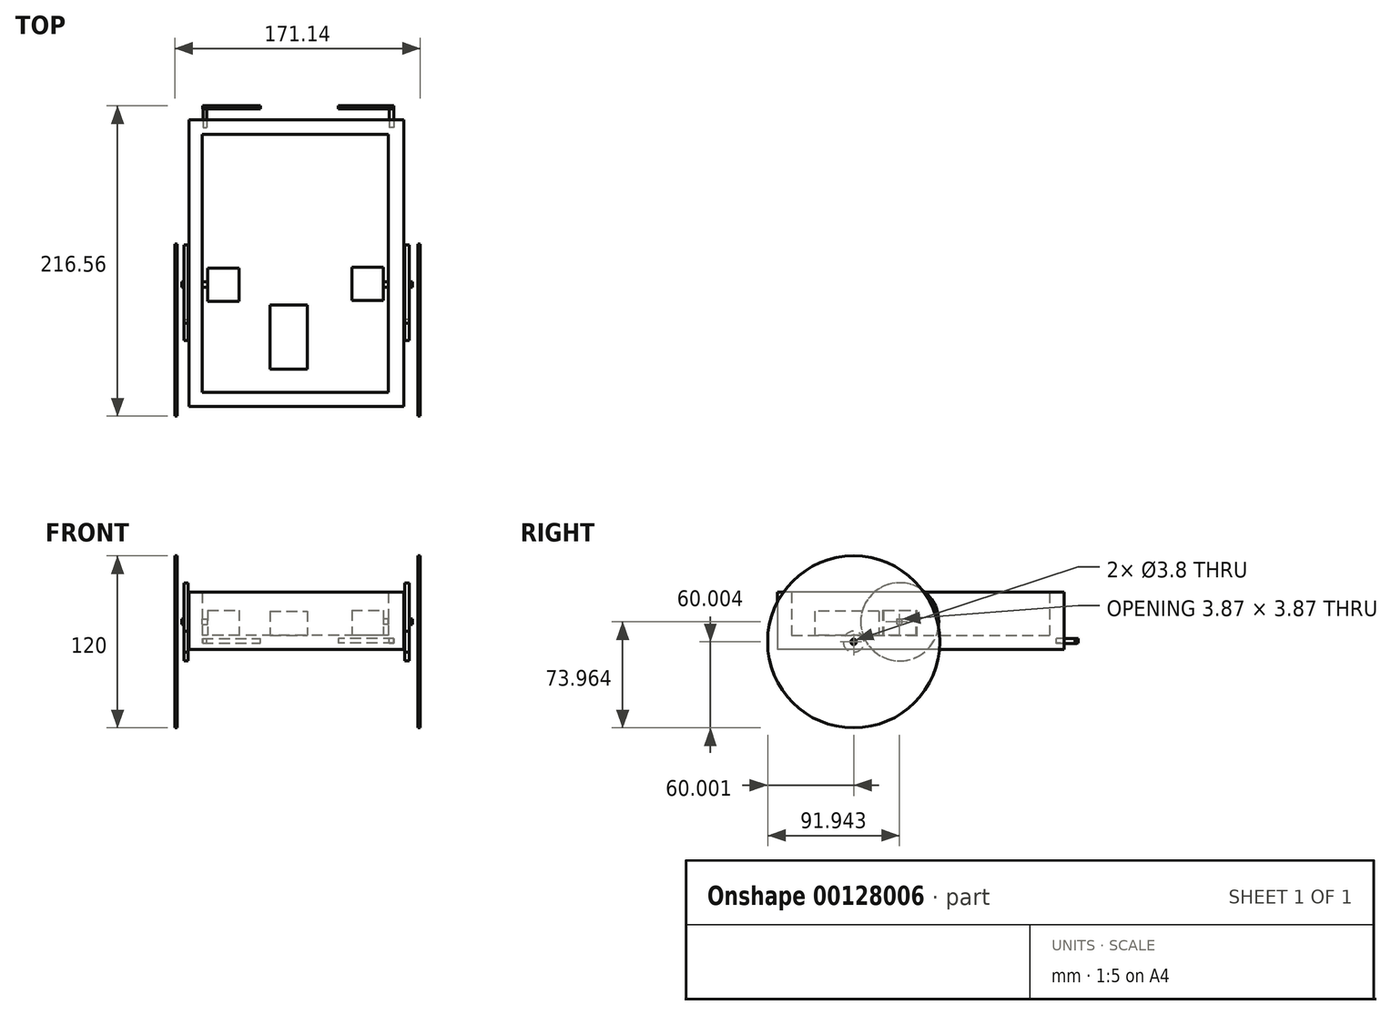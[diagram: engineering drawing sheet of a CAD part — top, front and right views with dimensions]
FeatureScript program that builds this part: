
annotation { "Feature Type Name" : "Feature", "Feature Type Description" : "" }
export const myFeature = defineFeature(function(context is Context, id is Id, definition is map)
    precondition{}
    {
        {
            var Q0;
            Q0=qCreatedBy(makeId("Top.planeOp"),FACE);
            var sketch = newSketch(context, id + "F0", { "sketchPlane" : qUnion([Q0])});
            skLineSegment(sketch, "E0.bottom", {"start": v(-84.27, 106.29) * mm, "end": v(65.73, 106.29) * mm});
            skLineSegment(sketch, "E0.top", {"start": v(-84.27, -93.71) * mm, "end": v(65.73, -93.71) * mm});
            skLineSegment(sketch, "E0.left", {"start": v(-84.27, 106.29) * mm, "end": v(-84.27, -93.71) * mm});
            skLineSegment(sketch, "E0.right", {"start": v(65.73, 106.29) * mm, "end": v(65.73, -93.71) * mm});
            skLineSegment(sketch, "E1.bottom", {"start": v(-75, 96.1) * mm, "end": v(55, 96.1) * mm});
            skLineSegment(sketch, "E1.top", {"start": v(-75, -83.9) * mm, "end": v(55, -83.9) * mm});
            skLineSegment(sketch, "E1.left", {"start": v(-75, 96.1) * mm, "end": v(-75, -83.9) * mm});
            skLineSegment(sketch, "E1.right", {"start": v(55, 96.1) * mm, "end": v(55, -83.9) * mm});
            skLineSegment(sketch, "E2.bottom", {"start": v(-27.63, -23.08) * mm, "end": v(-1.63, -23.08) * mm});
            skLineSegment(sketch, "E2.top", {"start": v(-27.63, -67.78) * mm, "end": v(-1.63, -67.78) * mm});
            skLineSegment(sketch, "E2.left", {"start": v(-27.63, -23.08) * mm, "end": v(-27.63, -67.78) * mm});
            skLineSegment(sketch, "E2.right", {"start": v(-1.63, -23.08) * mm, "end": v(-1.63, -67.78) * mm});
            skSolve(sketch);
        }
        {
            var Q0;
            Q0=makeQuery(id+"F0.imprint","IMPRINT",FACE,{"disambiguationData":[TD([[makeQuery(id+"F0.imprint","IMPRINT",EDGE,{"derivedFrom":sQuery(id+"F0.wireOp",EDGE,"E1.bottom")}),-1.0]])]});
            var Q1;
            Q1=makeQuery(id+"F0.imprint","IMPRINT",FACE,{"disambiguationData":[TD([[makeQuery(id+"F0.imprint","IMPRINT",EDGE,{"derivedFrom":sQuery(id+"F0.wireOp",EDGE,"E0.bottom")}),-1.0]])]});
            extrude(context, id + "F1", {"entities" : qUnion([Q0, Q1]), "depth" : 10 * mm});
        }
        {
            var Q0;
            Q0=qCreatedBy(makeId("Right.planeOp"),FACE);
            var sketch = newSketch(context, id + "F2", { "sketchPlane" : qUnion([Q0])});
            skCircle(sketch, "E3", {"center": v(-40.59, 5.37) * mm, "radius": 60 * mm});
            skCircle(sketch, "E4", {"center": v(-40.59, 5.37) * mm, "radius": 1.9 * mm});
            skSolve(sketch);
        }
        {
            var Q0;
            Q0 = qSketchRegion(id + "F2", true);
            extrude(context, id + "F3", {"entities" : qUnion([Q0]), "depth" : 77.18 * mm, "hasSecondDirection" : true, "secondDirectionOppositeDirection" : false, "secondDirectionDepth" : 75.66 * mm});
        }
        {
            var Q0;
            Q0=sQuery(id+"F2.wireOp",EDGE,"E4");
            extrude(context, id + "F4", {"bodyType" : ToolBodyType.SURFACE, "surfaceEntities" : qUnion([Q0]), "depth" : 77.33 * mm});
        }
        {
            var Q0;
            Q0=sQuery(id+"F2.wireOp",EDGE,"E4");
            extrude(context, id + "F5", {"bodyType" : ToolBodyType.SURFACE, "surfaceEntities" : qUnion([Q0]), "oppositeDirection" : true, "depth" : 94.58 * mm});
        }
        {
            var Q0;
            Q0=qCreatedBy(makeId("Right.planeOp"),FACE);
            var sketch = newSketch(context, id + "F6", { "sketchPlane" : qUnion([Q0])});
            skCircle(sketch, "E5", {"center": v(-8.65, 19.33) * mm, "radius": 1.93 * mm});
            skSolve(sketch);
        }
        {
            var Q0;
            Q0=makeQuery(id+"F6.imprint","IMPRINT",FACE,{"disambiguationData":[TD([[makeQuery(id+"F6.imprint","IMPRINT",EDGE,{"derivedFrom":sQuery(id+"F6.wireOp",EDGE,"E5")}),1.0]])]});
            extrude(context, id + "F7", {"entities" : qUnion([Q0]), "operationType" : NewBodyOperationType.ADD, "depth" : 71.67 * mm, "hasSecondDirection" : true, "secondDirectionOppositeDirection" : false, "secondDirectionDepth" : 44.25 * mm});
        }
        {
            var Q0;
            Q0=makeQuery(id+"F6.imprint","IMPRINT",FACE,{"disambiguationData":[TD([[makeQuery(id+"F6.imprint","IMPRINT",EDGE,{"derivedFrom":sQuery(id+"F6.wireOp",EDGE,"E5")}),1.0]])]});
            extrude(context, id + "F8", {"entities" : qUnion([Q0]), "operationType" : NewBodyOperationType.ADD, "oppositeDirection" : true, "depth" : 89.14 * mm, "hasSecondDirection" : true, "secondDirectionOppositeDirection" : true, "secondDirectionDepth" : 63.4 * mm});
        }
        {
            var Q0;
            Q0=qCreatedBy(makeId("Right.planeOp"),FACE);
            var sketch = newSketch(context, id + "F9", { "sketchPlane" : qUnion([Q0])});
            skCircle(sketch, "E6", {"center": v(-8.41, 19.33) * mm, "radius": 27.23 * mm});
            skCircle(sketch, "E7", {"center": v(-40.56, 5.5) * mm, "radius": 7.29 * mm});
            skSolve(sketch);
        }
        {
            var Q0;
            Q0=qCreatedBy(makeId("Top.planeOp"),FACE);
            var sketch = newSketch(context, id + "F10", { "sketchPlane" : qUnion([Q0])});
            skLineSegment(sketch, "E8.bottom", {"start": v(-71.1, -20.36) * mm, "end": v(-49.1, -20.36) * mm});
            skLineSegment(sketch, "E8.top", {"start": v(-71.1, 2.84) * mm, "end": v(-49.1, 2.84) * mm});
            skLineSegment(sketch, "E8.left", {"start": v(-71.1, -20.36) * mm, "end": v(-71.1, 2.84) * mm});
            skLineSegment(sketch, "E8.right", {"start": v(-49.1, -20.36) * mm, "end": v(-49.1, 2.84) * mm});
            skLineSegment(sketch, "E9.bottom", {"start": v(29.42, -19.83) * mm, "end": v(51.42, -19.83) * mm});
            skLineSegment(sketch, "E9.top", {"start": v(29.42, 3.37) * mm, "end": v(51.42, 3.37) * mm});
            skLineSegment(sketch, "E9.left", {"start": v(29.42, -19.83) * mm, "end": v(29.42, 3.37) * mm});
            skLineSegment(sketch, "E9.right", {"start": v(51.42, -19.83) * mm, "end": v(51.42, 3.37) * mm});
            skPoint(sketch, "E10.endSnap0", {"position": v(-71.1, -8.76) * mm});
            skPoint(sketch, "E11.endSnap0", {"position": v(51.42, -8.23) * mm});
            skLineSegment(sketch, "E12.left", {"start": v(-71.1, -7.2) * mm, "end": v(-71.1, -9.84) * mm});
            skLineSegment(sketch, "E12.right", {"start": v(-87.63, -7.2) * mm, "end": v(-87.63, -9.84) * mm});
            skPoint(sketch, "E11.start.orphan", {"position": v(51.42, -8.23) * mm});
            skPoint(sketch, "E10.start.orphan", {"position": v(-71.1, -8.76) * mm});
            skSolve(sketch);
        }
        {
            var Q0;
            Q0 = qSketchRegion(id + "F10", true);
            extrude(context, id + "F11", {"entities" : qUnion([Q0]), "operationType" : NewBodyOperationType.ADD, "depth" : 27.5 * mm});
        }
        {
            var Q0;
            Q0=makeQuery(id+"F0.imprint","IMPRINT",FACE,{"disambiguationData":[TD([[makeQuery(id+"F0.imprint","IMPRINT",EDGE,{"derivedFrom":sQuery(id+"F0.wireOp",EDGE,"E0.bottom")}),-1.0]])]});
            extrude(context, id + "F12", {"entities" : qUnion([Q0]), "operationType" : NewBodyOperationType.ADD, "depth" : 40 * mm});
        }
        {
            var Q0;
            Q0=makeQuery(id+"F2.imprint","IMPRINT",FACE,{"disambiguationData":[TD([[makeQuery(id+"F2.imprint","IMPRINT",EDGE,{"derivedFrom":sQuery(id+"F2.wireOp",EDGE,"E3")}),1.0]])]});
            extrude(context, id + "F13", {"entities" : qUnion([Q0]), "oppositeDirection" : true, "depth" : 93.96 * mm, "hasSecondDirection" : true, "secondDirectionOppositeDirection" : true, "secondDirectionDepth" : 92.38 * mm});
        }
        {
            var Q0;
            Q0=makeQuery(id+"F0.imprint","IMPRINT",FACE,{"disambiguationData":[TD([[makeQuery(id+"F0.imprint","IMPRINT",EDGE,{"derivedFrom":sQuery(id+"F0.wireOp",EDGE,"E2.bottom")}),-1.0]])]});
            extrude(context, id + "F14", {"entities" : qUnion([Q0]), "operationType" : NewBodyOperationType.ADD, "depth" : 26.9 * mm});
        }
        {
            var Q0;
            Q0 = qSketchRegion(id + "F9", true);
            extrude(context, id + "F15", {"entities" : qUnion([Q0]), "operationType" : NewBodyOperationType.ADD, "depth" : 69.67 * mm, "hasSecondDirection" : true, "secondDirectionOppositeDirection" : false, "secondDirectionDepth" : 66.37 * mm});
        }
        {
            var Q0;
            Q0 = qSketchRegion(id + "F9", true);
            extrude(context, id + "F16", {"entities" : qUnion([Q0]), "operationType" : NewBodyOperationType.ADD, "oppositeDirection" : true, "depth" : 87.63 * mm, "hasSecondDirection" : true, "secondDirectionOppositeDirection" : true, "secondDirectionDepth" : 84.75 * mm});
        }
        {
            var Q0;
            Q0=qCreatedBy(makeId("Front.planeOp"),FACE);
            var sketch = newSketch(context, id + "F17", { "sketchPlane" : qUnion([Q0])});
            skLineSegment(sketch, "E13.bottom", {"start": v(58.83, 7.6) * mm, "end": v(20.12, 7.6) * mm});
            skLineSegment(sketch, "E13.top", {"start": v(58.83, 4.66) * mm, "end": v(20.12, 4.66) * mm});
            skLineSegment(sketch, "E13.left", {"start": v(58.83, 7.6) * mm, "end": v(58.83, 4.66) * mm});
            skLineSegment(sketch, "E13.right", {"start": v(20.12, 7.6) * mm, "end": v(20.12, 4.66) * mm});
            skLineSegment(sketch, "E14.bottom", {"start": v(-74.68, 4.66) * mm, "end": v(-34.16, 4.66) * mm});
            skLineSegment(sketch, "E14.top", {"start": v(-74.68, 7.83) * mm, "end": v(-34.16, 7.83) * mm});
            skLineSegment(sketch, "E14.left", {"start": v(-74.68, 4.66) * mm, "end": v(-74.68, 7.83) * mm});
            skLineSegment(sketch, "E14.right", {"start": v(-34.16, 4.66) * mm, "end": v(-34.16, 7.83) * mm});
            skSolve(sketch);
        }
        {
            var Q0;
            Q0 = qSketchRegion(id + "F17", true);
            extrude(context, id + "F18", {"entities" : qUnion([Q0]), "oppositeDirection" : true, "depth" : 115.97 * mm, "hasSecondDirection" : true, "secondDirectionOppositeDirection" : true, "secondDirectionDepth" : 113.94 * mm});
        }
        {
            var Q0;
            Q0=qCreatedBy(makeId("Front.planeOp"),FACE);
            var sketch = newSketch(context, id + "F19", { "sketchPlane" : qUnion([Q0])});
            skLineSegment(sketch, "E15.bottom", {"start": v(58.83, 4.32) * mm, "end": v(55.55, 4.32) * mm});
            skLineSegment(sketch, "E15.top", {"start": v(58.83, 7.6) * mm, "end": v(55.55, 7.6) * mm});
            skLineSegment(sketch, "E15.left", {"start": v(58.83, 4.32) * mm, "end": v(58.83, 7.6) * mm});
            skLineSegment(sketch, "E15.right", {"start": v(55.55, 4.32) * mm, "end": v(55.55, 7.6) * mm});
            skLineSegment(sketch, "E16.bottom", {"start": v(-74.44, 4.55) * mm, "end": v(-71.86, 4.55) * mm});
            skLineSegment(sketch, "E16.top", {"start": v(-74.44, 7.6) * mm, "end": v(-71.86, 7.6) * mm});
            skLineSegment(sketch, "E16.left", {"start": v(-74.44, 4.55) * mm, "end": v(-74.44, 7.6) * mm});
            skLineSegment(sketch, "E16.right", {"start": v(-71.86, 4.55) * mm, "end": v(-71.86, 7.6) * mm});
            skSolve(sketch);
        }
        {
            var Q0;
            Q0 = qSketchRegion(id + "F19", true);
            extrude(context, id + "F20", {"entities" : qUnion([Q0]), "oppositeDirection" : true, "depth" : 115.12 * mm, "hasSecondDirection" : true, "secondDirectionOppositeDirection" : true, "secondDirectionDepth" : 100.74 * mm});
        }
    });
